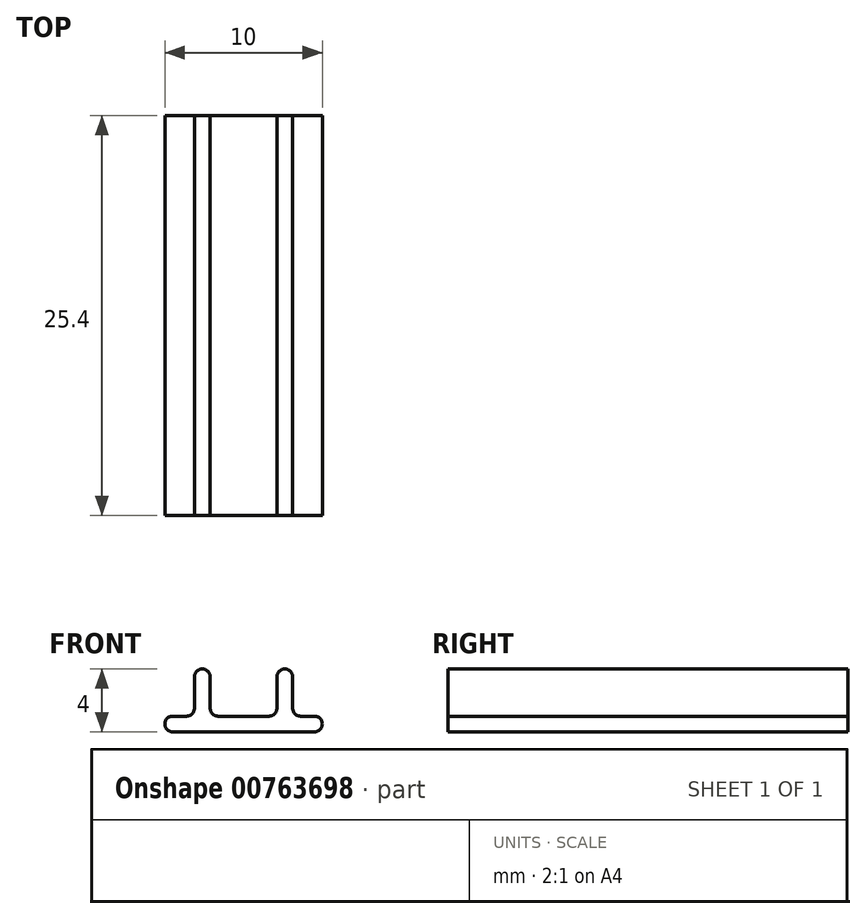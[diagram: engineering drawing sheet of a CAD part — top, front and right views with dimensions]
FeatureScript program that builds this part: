
annotation { "Feature Type Name" : "Feature", "Feature Type Description" : "" }
export const myFeature = defineFeature(function(context is Context, id is Id, definition is map)
    precondition{}
    {
        {
            var Q0;
            Q0=qCreatedBy(makeId("Front.planeOp"),FACE);
            var sketch = newSketch(context, id + "F0", { "sketchPlane" : qUnion([Q0])});
            skLineSegment(sketch, "E0.bottom", {"start": v(-4.5, 0.5) * mm, "end": v(-3.62, 0.5) * mm});
            skLineSegment(sketch, "E0.top", {"start": v(-4.5, -0.5) * mm, "end": v(4.5, -0.5) * mm});
            skLineSegment(sketch, "E0.left", {"start": v(-5, 0) * mm, "end": v(-5, 0) * mm});
            skLineSegment(sketch, "E0.right", {"start": v(5, 0) * mm, "end": v(5, 0) * mm});
            skPoint(sketch, "E0.middle", {"position": v(0, 0) * mm});
            skLineSegment(sketch, "E1.top", {"start": v(-2.62, 3.5) * mm, "end": v(-2.62, 3.5) * mm});
            skLineSegment(sketch, "E1.left", {"start": v(-2.12, 1) * mm, "end": v(-2.12, 3) * mm});
            skLineSegment(sketch, "E1.right", {"start": v(-3.12, 1) * mm, "end": v(-3.12, 3) * mm});
            skLineSegment(sketch, "E2", {"start": v(0, -0.5) * mm, "end": v(0, 5.52) * mm, "construction": true});
            skLineSegment(sketch, "E3.MirrorCS", {"start": v(2.12, 1) * mm, "end": v(2.12, 3) * mm});
            skLineSegment(sketch, "E4.MirrorCS", {"start": v(2.62, 3.5) * mm, "end": v(2.62, 3.5) * mm});
            skLineSegment(sketch, "E5.MirrorCS", {"start": v(3.12, 1) * mm, "end": v(3.12, 3) * mm});
            skLineSegment(sketch, "E6.trimOffspring", {"start": v(-1.62, 0.5) * mm, "end": v(1.62, 0.5) * mm});
            skLineSegment(sketch, "E7.trimOffspring", {"start": v(3.62, 0.5) * mm, "end": v(4.5, 0.5) * mm});
            skPoint(sketch, "E8.visualSharp", {"position": v(-3.12, 3.5) * mm});
            skArc(sketch, "E8.filletArc", {"start": v(-2.62, 3.5) * mm, "mid": v(-2.97, 3.35) * mm, "end": v(-3.12, 3) * mm});
            skPoint(sketch, "E9.visualSharp", {"position": v(-2.12, 3.5) * mm});
            skArc(sketch, "E9.filletArc", {"start": v(-2.12, 3) * mm, "mid": v(-2.27, 3.35) * mm, "end": v(-2.62, 3.5) * mm});
            skPoint(sketch, "E10.visualSharp", {"position": v(2.12, 3.5) * mm});
            skArc(sketch, "E10.filletArc", {"start": v(2.62, 3.5) * mm, "mid": v(2.27, 3.35) * mm, "end": v(2.12, 3) * mm});
            skPoint(sketch, "E11.visualSharp", {"position": v(3.12, 3.5) * mm});
            skArc(sketch, "E11.filletArc", {"start": v(3.12, 3) * mm, "mid": v(2.97, 3.35) * mm, "end": v(2.62, 3.5) * mm});
            skPoint(sketch, "E12.visualSharp", {"position": v(2.12, 0.5) * mm});
            skArc(sketch, "E12.filletArc", {"start": v(1.62, 0.5) * mm, "mid": v(1.97, 0.65) * mm, "end": v(2.12, 1) * mm});
            skPoint(sketch, "E13.visualSharp", {"position": v(-2.12, 0.5) * mm});
            skArc(sketch, "E13.filletArc", {"start": v(-2.12, 1) * mm, "mid": v(-1.97, 0.65) * mm, "end": v(-1.62, 0.5) * mm});
            skPoint(sketch, "E14.visualSharp", {"position": v(-3.12, 0.5) * mm});
            skArc(sketch, "E14.filletArc", {"start": v(-3.62, 0.5) * mm, "mid": v(-3.27, 0.65) * mm, "end": v(-3.12, 1) * mm});
            skPoint(sketch, "E15.visualSharp", {"position": v(3.12, 0.5) * mm});
            skArc(sketch, "E15.filletArc", {"start": v(3.12, 1) * mm, "mid": v(3.27, 0.65) * mm, "end": v(3.62, 0.5) * mm});
            skPoint(sketch, "E16.visualSharp", {"position": v(5, 0.5) * mm});
            skArc(sketch, "E16.filletArc", {"start": v(5, 0) * mm, "mid": v(4.85, 0.35) * mm, "end": v(4.5, 0.5) * mm});
            skPoint(sketch, "E17.visualSharp", {"position": v(5, -0.5) * mm});
            skArc(sketch, "E17.filletArc", {"start": v(4.5, -0.5) * mm, "mid": v(4.85, -0.35) * mm, "end": v(5, 0) * mm});
            skPoint(sketch, "E18.visualSharp", {"position": v(-5, 0.5) * mm});
            skArc(sketch, "E18.filletArc", {"start": v(-4.5, 0.5) * mm, "mid": v(-4.85, 0.35) * mm, "end": v(-5, 0) * mm});
            skPoint(sketch, "E19.visualSharp", {"position": v(-5, -0.5) * mm});
            skArc(sketch, "E19.filletArc", {"start": v(-5, 0) * mm, "mid": v(-4.85, -0.35) * mm, "end": v(-4.5, -0.5) * mm});
            skSolve(sketch);
        }
        {
            var Q0;
            Q0=makeQuery(id+"F0.imprint","IMPRINT",FACE,{"disambiguationData":[TD([[makeQuery(id+"F0.imprint","IMPRINT",EDGE,{"derivedFrom":sQuery(id+"F0.wireOp",EDGE,"E0.bottom")}),-1.0]])]});
            extrude(context, id + "F1", {"entities" : qUnion([Q0]), "endBound" : BoundingType.SYMMETRIC, "depth" : 25.4 * mm, "offsetDistance" : 25.4 * mm});
        }
    });
